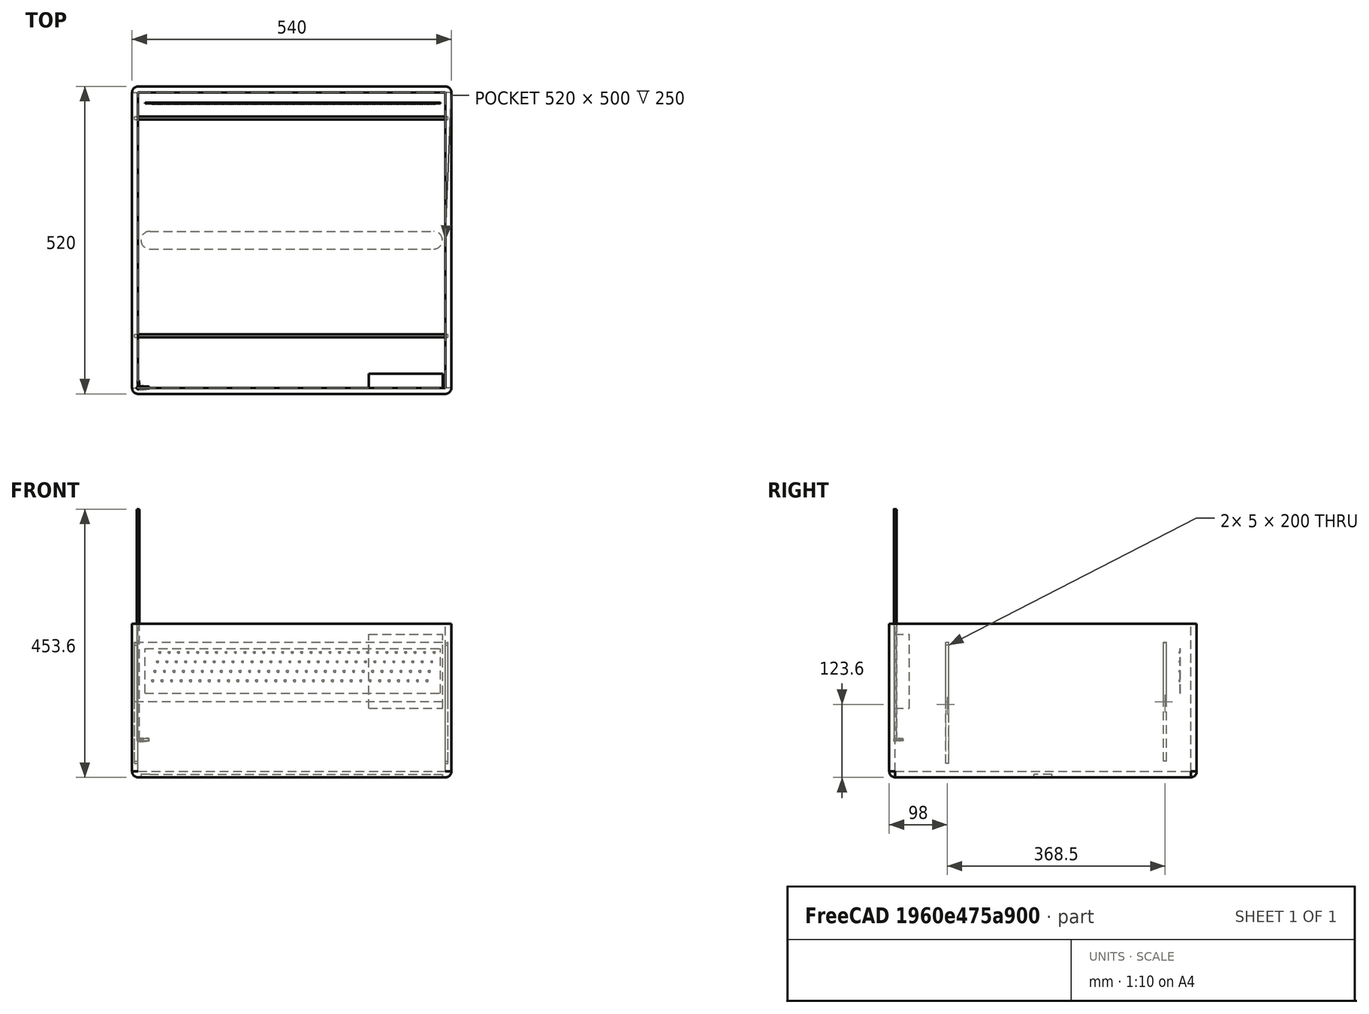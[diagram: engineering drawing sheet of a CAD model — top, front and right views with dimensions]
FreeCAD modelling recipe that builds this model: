
FCSTD DOCUMENT  (FreeCAD 0.20RUnknown)
Label: CherenkovBoxTechnicalNote22February22
License: All rights reserved
LicenseURL: http://en.wikipedia.org/wiki/All_rights_reserved
objects: Part::Part2DObjectPython×16, Part::Box×13, App::Part×13, Part::Compound×10, Part::Sweep×8, App::FeaturePython×7, Part::Feature×6, Part::FeaturePython×4, Part::Cut×3, Part::Thickness×1, Sketcher::SketchObject×1, Part::Extrusion×1
note: 59 computed .brp shape members not serialized (recipe doc carries the construction recipe); baked Part::Feature solids carry a one-line shape summary decoded from their .brp

FEATURE [Part::Box] Box001  label="Support001"
  AttacherType = Attacher::AttachEngine3D
  Height = 100
  Length = 530
  Placement = pos=(-5.7935,85.5,65) rot=(0,0,1;0rad)
  Width = 5
FEATURE [Part::Box] Box002  label="Support002"
  AttacherType = Attacher::AttachEngine3D
  Height = 100
  Length = 530
  Placement = pos=(-5.7935,454,65) rot=(0,0,1;0rad)
  Width = 5
FEATURE [Part::Box] Box008  label="SiPM"
  AttacherType = Attacher::AttachEngine3D
  Height = 3
  Length = 3
  Width = 1
FEATURE [Part::FeaturePython] Array001  label="SiPM001"  # Draft array (typed FeaturePython)
  Angle = 360
  ArrayType = 0
  Axis = (0,0,1)
  Base = -> Box008
  Center = (0,0,0)
  Count = 120
  ExpandArray = false
  Fuse = false
  IntervalAxis = (0,0,0)
  IntervalX = (16,0,0)
  IntervalY = (4,0,16)
  IntervalZ = (0,0,100)
  NumberCircles = 3
  NumberPolar = 5
  NumberX = 30
  NumberY = 4
  NumberZ = 1
  Placement = pos=(23.5,479,98.5) rot=(0,0,1;0rad)
  PlacementList = 120 placements: [(0,0,0),(4,0,16),(8,0,32),(12,0,48),(16,0,0),(20,0,16),(24,0,32),(28,0,48),(32,0,0),(36,0,16),(40,0,32),(44,0,48),(48,0,0),(52,0,16),(56,0,32),(60,0,48),(64,0,0),(68,0,16),(72,0,32),(76,0,48),(80,0,0),(84,0,16),(88,0,32),(92,0,48),(96,0,0),(100,0,16),(104,0,32),(108,0,48),(112,0,0),(116,0,16),(120,0,32),(124,0,48),(128,0,0),(132,0,16),(136,0,32),(140,0,48),(144,0,0),(148,0,16),(152,0,32),+81 more]
  RadialDistance = 50
  ScaleList = (120) [(1,1,1),(1,1,1),(1,1,1),(1,1,1),(1,1,1),(1,1,1),(1,1,1),(1,1,1),(1,1,1),(1,1,1),(1,1,1),(1,1,1),(1,1,1),(1,1,1),(1,1,1),(1,1,1),(1,1,1),(1,1,1),+102 more]
  Symmetry = 1
  TangentialDistance = 25
FEATURE [Part::Box] Box009  label="PCB"
  AttacherType = Attacher::AttachEngine3D
  Height = 75
  Length = 500
  Placement = pos=(11.7065,480,79) rot=(0,0,1;0rad)
  Width = 1
FEATURE [Part::Compound] Compound  label="PCBSiPM"
  Links = -> [Box009,Array001]
  Placement = pos=(0,1.6,0) rot=(0,0,1;0rad)
FEATURE [Part::Feature] Part__Feature003  label="SmallEndCapModel"
  shape: bbox 4.6 x 13 x 4.6 mm, 17 faces (baked)
FEATURE [Part::Feature] Part__Feature004  label="BigEndcapModel"
  shape: bbox 18 x 5.9 x 5.9 mm, 16 faces (baked)
FEATURE [App::Part] SmallEndCap001
  Group = -> [Part__Feature003]
  Origin = -> Origin005
  Placement = pos=(0,0,-8.5) rot=(1,0,0;1.5708rad)
FEATURE [Part::Feature] Part__Feature005  label="StrawTubeModel001"
  shape: bbox 4.15 x 4.15 x 390 mm, 4 faces (baked)
FEATURE [App::Part] StrawTube001
  Group = -> [Part__Feature005]
  Origin = -> Origin
FEATURE [App::Part] BigEndCap001
  Group = -> [Part__Feature004]
  Origin = -> Origin006
  Placement = pos=(0,0,405.5) rot=(0,1,0;1.5708rad)
FEATURE [App::Part] Straw
  Group = -> [StrawTube001,SmallEndCap001,BigEndCap001]
  Origin = -> Origin007
  Placement = pos=(0,0,0) rot=(1,0,0;4.71239rad)
FEATURE [Part::FeaturePython] Array002  label="ArrayStraws"  # Draft array (typed FeaturePython)
  Angle = 360
  ArrayType = 0
  Axis = (0,0,1)
  Base = -> Straw
  Center = (0,0,0)
  Count = 120
  ExpandArray = false
  Fuse = false
  IntervalAxis = (0,0,0)
  IntervalX = (16,0,0)
  IntervalY = (4,0,16)
  IntervalZ = (0,0,100)
  NumberCircles = 3
  NumberPolar = 5
  NumberX = 30
  NumberY = 4
  NumberZ = 1
  Placement = pos=(25,75,100) rot=(0,0,1;0rad)
  PlacementList = <same value as first occurrence — deduplicated (x4 in doc)>
  RadialDistance = 50
  ScaleList = (120) [(1,1,1),(1,1,1),(1,1,1),(1,1,1),(1,1,1),(1,1,1),(1,1,1),(1,1,1),(1,1,1),(1,1,1),(1,1,1),(1,1,1),(1,1,1),(1,1,1),(1,1,1),(1,1,1),(1,1,1),(1,1,1),+102 more]
  Symmetry = 1
  TangentialDistance = 25
FEATURE [Part::Part2DObjectPython] BezCurve004  # Draft 2D object (typed FeaturePython)
  Area = 0
  Closed = false
  Degree = 3
  Length = 133.246
  MakeFace = true
  Points = (4) [(37.73,178.199,85.1424),(15,143.338,83.3527),(-3.29845,149.367,143.96),(39.5292,81.953,149.244)]
FEATURE [Part::Part2DObjectPython] Circle005  # Draft 2D object (typed FeaturePython)
  Area = 0.785398
  FirstAngle = 0
  LastAngle = 0
  MakeFace = true
  Placement = pos=(39.5292,81.953,149.244) rot=(-0.540873,0.659298,0.522286;3.71755rad)
  Radius = 0.5
FEATURE [Part::Part2DObjectPython] BezCurve005  # Draft 2D object (typed FeaturePython)
  Area = 0
  Closed = false
  Degree = 3
  Length = 133.246
  MakeFace = true
  Points = (4) [(37.73,178.199,85.1424),(15,143.338,83.3527),(-3.29845,149.367,143.96),(39.5292,81.953,149.244)]
FEATURE [Part::Box] Box013  label="CalibLEDBox001"
  AttacherType = Attacher::AttachEngine3D
  Height = 25
  Length = 125
  Placement = pos=(390.26,-0.9,53.5) rot=(0.57735,0.57735,0.57735;4.18879rad)
  Width = 125
FEATURE [Part::Part2DObjectPython] BezCurve006  # Draft 2D object (typed FeaturePython)
  Area = 0
  Closed = false
  Degree = 3
  Length = 133.246
  MakeFace = true
  Points = (4) [(37.73,178.199,85.1424),(15,143.338,83.3527),(-3.29845,149.367,143.96),(39.5292,81.953,149.244)]
FEATURE [Part::Part2DObjectPython] Circle006  # Draft 2D object (typed FeaturePython)
  Area = 0.785398
  FirstAngle = 0
  LastAngle = 0
  MakeFace = true
  Placement = pos=(39.5292,81.953,149.244) rot=(-0.540873,0.659298,0.522286;3.71755rad)
  Radius = 0.5
FEATURE [Part::Sweep] Sweep006  label="OpticFiber007"
  Frenet = false
  Placement = pos=(-83.0642,-149.15,32.7197) rot=(-0.889126,-0.323616,-0.323616;1.68804rad)
  Sections = -> [Circle006]
  Solid = false
  Spine = -> BezCurve006 [Edge1]
  Transition = 1
FEATURE [Part::Compound] Compound008  label="Fiber008"
  Links = -> [Sweep006]
  Placement = pos=(538,81,98.5) rot=(0.57735,0.57735,0.57735;4.18879rad)
FEATURE [Part::Part2DObjectPython] BezCurve007  # Draft 2D object (typed FeaturePython)
  Area = 0
  Closed = false
  Degree = 3
  Length = 133.246
  MakeFace = true
  Points = (4) [(37.73,178.199,85.1424),(15,143.338,83.3527),(-3.29845,149.367,143.96),(39.5292,81.953,149.244)]
FEATURE [Part::Sweep] Sweep005  label="OpticFiber006"
  Frenet = false
  Placement = pos=(-83.0642,-149.15,32.7197) rot=(-0.889126,-0.323616,-0.323616;1.68804rad)
  Sections = -> [Circle005]
  Solid = false
  Spine = -> BezCurve007 [Edge1]
  Transition = 1
FEATURE [Part::Compound] Compound007  label="Fiber007"
  Links = -> [Sweep005]
  Placement = pos=(553.7,81,98.2) rot=(0.57735,0.57735,0.57735;4.18879rad)
FEATURE [Part::Part2DObjectPython] Circle007  # Draft 2D object (typed FeaturePython)
  Area = 0.785398
  FirstAngle = 0
  LastAngle = 0
  MakeFace = true
  Placement = pos=(39.5292,81.953,149.244) rot=(-0.540873,0.659298,0.522286;3.71755rad)
  Radius = 0.5
FEATURE [Part::Sweep] Sweep007  label="OpticFiber008"
  Frenet = false
  Placement = pos=(-83.0642,-149.15,32.7197) rot=(-0.889126,-0.323616,-0.323616;1.68804rad)
  Sections = -> [Circle007]
  Solid = false
  Spine = -> BezCurve004 [Edge1]
  Transition = 1
FEATURE [Part::Compound] Compound006  label="Fiber006"
  Links = -> [Sweep007]
  Placement = pos=(558,81,115) rot=(0.57735,0.57735,0.57735;4.18879rad)
FEATURE [Part::Part2DObjectPython] Circle008  # Draft 2D object (typed FeaturePython)
  Area = 0.785398
  FirstAngle = 0
  LastAngle = 0
  MakeFace = true
  Placement = pos=(39.5292,81.953,149.244) rot=(-0.540873,0.659298,0.522286;3.71755rad)
  Radius = 0.5
FEATURE [Part::Sweep] Sweep004  label="OpticFiber005"
  Frenet = false
  Placement = pos=(-83.0642,-149.15,32.7197) rot=(-0.889126,-0.323616,-0.323616;1.68804rad)
  Sections = -> [Circle008]
  Solid = false
  Spine = -> BezCurve005 [Edge1]
  Transition = 1
FEATURE [Part::Compound] Compound005  label="Fiber005"
  Links = -> [Sweep004]
  Placement = pos=(542,81,115) rot=(0.57735,0.57735,0.57735;4.18879rad)
FEATURE [App::Part] Part  label="Fiber"
  Group = -> [Box013,Circle008,BezCurve005,Sweep004,Compound005,Circle007,BezCurve004,Sweep007,Compound006,Sweep005,Circle005,BezCurve007,Compound007,Circle006,Sweep006,BezCurve006,Compound008]
  Origin = -> Origin008
  Placement = pos=(-268.1,0,0) rot=(0,0,1;0rad)
FEATURE [App::Part] Part001  label="SiPMReadout"
  Group = -> [Straw,Array002,Part,Box008,Array001,Box009,Compound,Box002,Box001]
  Origin = -> Origin009
FEATURE [Part::Part2DObjectPython] Circle009  # Draft 2D object (typed FeaturePython)
  Area = 0.785398
  FirstAngle = 0
  LastAngle = 0
  MakeFace = true
  Placement = pos=(39.5292,81.953,149.244) rot=(-0.540873,0.659298,0.522286;3.71755rad)
  Radius = 0.5
FEATURE [Part::Box] Box014  label="SiPM002"
  AttacherType = Attacher::AttachEngine3D
  Height = 3
  Length = 3
  Width = 1
FEATURE [Part::FeaturePython] Array003  label="SiPM003"  # Draft array (typed FeaturePython)
  Angle = 360
  ArrayType = 0
  Axis = (0,0,1)
  Base = -> Box014
  Center = (0,0,0)
  Count = 120
  ExpandArray = false
  Fuse = false
  IntervalAxis = (0,0,0)
  IntervalX = (16,0,0)
  IntervalY = (4,0,16)
  IntervalZ = (0,0,100)
  NumberCircles = 3
  NumberPolar = 5
  NumberX = 30
  NumberY = 4
  NumberZ = 1
  Placement = pos=(23.5,479,98.5) rot=(0,0,1;0rad)
  PlacementList = <same value as first occurrence — deduplicated (x4 in doc)>
  RadialDistance = 50
  ScaleList = (120) [(1,1,1),(1,1,1),(1,1,1),(1,1,1),(1,1,1),(1,1,1),(1,1,1),(1,1,1),(1,1,1),(1,1,1),(1,1,1),(1,1,1),(1,1,1),(1,1,1),(1,1,1),(1,1,1),(1,1,1),(1,1,1),+102 more]
  Symmetry = 1
  TangentialDistance = 25
FEATURE [Part::Part2DObjectPython] Circle010  # Draft 2D object (typed FeaturePython)
  Area = 0.785398
  FirstAngle = 0
  LastAngle = 0
  MakeFace = true
  Placement = pos=(39.5292,81.953,149.244) rot=(-0.540873,0.659298,0.522286;3.71755rad)
  Radius = 0.5
FEATURE [Part::Part2DObjectPython] Circle011  # Draft 2D object (typed FeaturePython)
  Area = 0.785398
  FirstAngle = 0
  LastAngle = 0
  MakeFace = true
  Placement = pos=(39.5292,81.953,149.244) rot=(-0.540873,0.659298,0.522286;3.71755rad)
  Radius = 0.5
FEATURE [Part::Part2DObjectPython] BezCurve008  # Draft 2D object (typed FeaturePython)
  Area = 0
  Closed = false
  Degree = 3
  Length = 133.246
  MakeFace = true
  Points = (4) [(37.73,178.199,85.1424),(15,143.338,83.3527),(-3.29845,149.367,143.96),(39.5292,81.953,149.244)]
FEATURE [Part::Part2DObjectPython] Circle012  # Draft 2D object (typed FeaturePython)
  Area = 0.785398
  FirstAngle = 0
  LastAngle = 0
  MakeFace = true
  Placement = pos=(39.5292,81.953,149.244) rot=(-0.540873,0.659298,0.522286;3.71755rad)
  Radius = 0.5
FEATURE [Part::Part2DObjectPython] BezCurve009  # Draft 2D object (typed FeaturePython)
  Area = 0
  Closed = false
  Degree = 3
  Length = 133.246
  MakeFace = true
  Points = (4) [(37.73,178.199,85.1424),(15,143.338,83.3527),(-3.29845,149.367,143.96),(39.5292,81.953,149.244)]
FEATURE [Part::Sweep] Sweep008  label="OpticFiber009"
  Frenet = false
  Placement = pos=(-83.0642,-149.15,32.7197) rot=(-0.889126,-0.323616,-0.323616;1.68804rad)
  Sections = -> [Circle012]
  Solid = false
  Spine = -> BezCurve009 [Edge1]
  Transition = 1
FEATURE [Part::Compound] Compound009  label="Fiber009"
  Links = -> [Sweep008]
  Placement = pos=(553.7,81,98.2) rot=(0.57735,0.57735,0.57735;4.18879rad)
FEATURE [Part::Box] Box015  label="CalibLEDBox002"
  AttacherType = Attacher::AttachEngine3D
  Height = 25
  Length = 125
  Placement = pos=(390.26,-0.9,53.5) rot=(0.57735,0.57735,0.57735;4.18879rad)
  Width = 125
FEATURE [Part::Part2DObjectPython] BezCurve010  # Draft 2D object (typed FeaturePython)
  Area = 0
  Closed = false
  Degree = 3
  Length = 133.246
  MakeFace = true
  Points = (4) [(37.73,178.199,85.1424),(15,143.338,83.3527),(-3.29845,149.367,143.96),(39.5292,81.953,149.244)]
FEATURE [Part::Sweep] Sweep009  label="OpticFiber010"
  Frenet = false
  Placement = pos=(-83.0642,-149.15,32.7197) rot=(-0.889126,-0.323616,-0.323616;1.68804rad)
  Sections = -> [Circle010]
  Solid = false
  Spine = -> BezCurve010 [Edge1]
  Transition = 1
FEATURE [Part::Compound] Compound010  label="Fiber010"
  Links = -> [Sweep009]
  Placement = pos=(538,81,98.5) rot=(0.57735,0.57735,0.57735;4.18879rad)
FEATURE [Part::Sweep] Sweep010  label="OpticFiber011"
  Frenet = false
  Placement = pos=(-83.0642,-149.15,32.7197) rot=(-0.889126,-0.323616,-0.323616;1.68804rad)
  Sections = -> [Circle011]
  Solid = false
  Spine = -> BezCurve008 [Edge1]
  Transition = 1
FEATURE [Part::Compound] Compound012  label="Fiber012"
  Links = -> [Sweep010]
  Placement = pos=(558,81,115) rot=(0.57735,0.57735,0.57735;4.18879rad)
FEATURE [Part::Part2DObjectPython] BezCurve011  # Draft 2D object (typed FeaturePython)
  Area = 0
  Closed = false
  Degree = 3
  Length = 133.246
  MakeFace = true
  Points = (4) [(37.73,178.199,85.1424),(15,143.338,83.3527),(-3.29845,149.367,143.96),(39.5292,81.953,149.244)]
FEATURE [Part::Sweep] Sweep011  label="OpticFiber012"
  Frenet = false
  Placement = pos=(-83.0642,-149.15,32.7197) rot=(-0.889126,-0.323616,-0.323616;1.68804rad)
  Sections = -> [Circle009]
  Solid = false
  Spine = -> BezCurve011 [Edge1]
  Transition = 1
FEATURE [Part::Compound] Compound011  label="Fiber011"
  Links = -> [Sweep011]
  Placement = pos=(542,81,115) rot=(0.57735,0.57735,0.57735;4.18879rad)
FEATURE [Part::Box] Box016  label="Support003"
  AttacherType = Attacher::AttachEngine3D
  Height = 100
  Length = 530
  Placement = pos=(-5.7935,454,65) rot=(0,0,1;0rad)
  Width = 5
FEATURE [Part::Box] Box017  label="Support004"
  AttacherType = Attacher::AttachEngine3D
  Height = 100
  Length = 530
  Placement = pos=(-5.7935,85.5,65) rot=(0,0,1;0rad)
  Width = 5
FEATURE [App::Part] Part003  label="Fiber013"
  Group = -> [Box015,Circle009,BezCurve011,Sweep011,Compound011,Circle011,BezCurve008,Sweep010,Compound012,Sweep008,Circle012,BezCurve009,Compound009,Circle010,Sweep009,BezCurve010,Compound010]
  Origin = -> Origin012
  Placement = pos=(-112.9,0,0.6) rot=(0,0,1;0rad)
FEATURE [Part::Feature] Part__Feature006  label="SmallEndCapModel001"
  shape: bbox 4.6 x 13 x 4.6 mm, 17 faces (baked)
FEATURE [Part::Feature] Part__Feature007  label="BigEndcapModel001"
  shape: bbox 18 x 5.9 x 5.9 mm, 16 faces (baked)
FEATURE [App::Part] BigEndCap002
  Group = -> [Part__Feature007]
  Origin = -> Origin011
  Placement = pos=(0,0,405.5) rot=(0,1,0;1.5708rad)
FEATURE [Part::Box] Box018  label="PCB001"
  AttacherType = Attacher::AttachEngine3D
  Height = 75
  Length = 500
  Placement = pos=(11.7065,480,79) rot=(0,0,1;0rad)
  Width = 1
FEATURE [Part::Compound] Compound013  label="PCBSiPM001"
  Links = -> [Box018,Array003]
  Placement = pos=(0,1.6,0) rot=(0,0,1;0rad)
FEATURE [App::Part] SmallEndCap002
  Group = -> [Part__Feature006]
  Origin = -> Origin013
  Placement = pos=(0,0,-8.5) rot=(1,0,0;1.5708rad)
FEATURE [Part::Feature] Part__Feature008  label="StrawTubeModel002"
  shape: bbox 4.15 x 4.15 x 390 mm, 4 faces (baked)
FEATURE [App::Part] StrawTube002
  Group = -> [Part__Feature008]
  Origin = -> Origin015
FEATURE [App::Part] Straw001
  Group = -> [StrawTube002,SmallEndCap002,BigEndCap002]
  Origin = -> Origin014
  Placement = pos=(0,0,0) rot=(1,0,0;4.71239rad)
FEATURE [Part::FeaturePython] Array004  label="ArrayStraws001"  # Draft array (typed FeaturePython)
  Angle = 360
  ArrayType = 0
  Axis = (0,0,1)
  Base = -> Straw001
  Center = (0,0,0)
  Count = 120
  ExpandArray = false
  Fuse = false
  IntervalAxis = (0,0,0)
  IntervalX = (16,0,0)
  IntervalY = (4,0,16)
  IntervalZ = (0,0,100)
  NumberCircles = 3
  NumberPolar = 5
  NumberX = 30
  NumberY = 4
  NumberZ = 1
  Placement = pos=(25,75,100) rot=(0,0,1;0rad)
  PlacementList = <same value as first occurrence — deduplicated (x4 in doc)>
  RadialDistance = 50
  ScaleList = (120) [(1,1,1),(1,1,1),(1,1,1),(1,1,1),(1,1,1),(1,1,1),(1,1,1),(1,1,1),(1,1,1),(1,1,1),(1,1,1),(1,1,1),(1,1,1),(1,1,1),(1,1,1),(1,1,1),(1,1,1),(1,1,1),+102 more]
  Symmetry = 1
  TangentialDistance = 25
FEATURE [App::Part] Part002  label="APDReadout"
  Group = -> [Straw001,Array004,Part003,Box014,Array003,Box018,Compound013,Box016,Box017]
  Origin = -> Origin010
  Placement = pos=(0,0,-101.3) rot=(0,0,1;0rad)
FEATURE [Part::Box] Box019  label="SupportRail003"
  AttacherType = Attacher::AttachEngine3D
  Height = 200
  Length = 530
  Placement = pos=(-5.7935,85.5,13.6) rot=(0,0,1;0rad)
  Width = 5
FEATURE [Part::Box] Box020  label="SupportRail004"
  AttacherType = Attacher::AttachEngine3D
  Height = 200
  Length = 530
  Placement = pos=(-5.7935,454,17.5) rot=(0,0,1;0rad)
  Width = 5
FEATURE [Part::Box] Box021  label="Cube003"
  AttacherType = Attacher::AttachEngine3D
  Height = 250
  Length = 520
  Width = 500
FEATURE [Part::Thickness] Thickness001  label="Box001"
  Faces = -> Box021 [Face6]
  Intersection = false
  Join = 0
  Mode = 0
  SelfIntersection = false
  Value = 10
FEATURE [Part::Cut] Cut003
  Base = -> Thickness001
  Tool = -> Box020
FEATURE [Part::Cut] Cut004  label="BoxAll001"
  Base = -> Cut003
  Placement = pos=(0,0,-53.6) rot=(0,0,1;0rad)
  Tool = -> Box019
FEATURE [Sketcher::SketchObject] Sketch
  FullyConstrained = true
  MapMode = 5
  Placement = pos=(0,0,-63.6) rot=(1,0,0;3.14159rad)
  Support = -> [Cut004]
  sketch-geometry (4):
    g0: LineSegment StartX=20 StartY=-235 StartZ=0 EndX=500 EndY=-235 EndZ=0
    g1: LineSegment StartX=20 StartY=-265 StartZ=0 EndX=500 EndY=-265 EndZ=0
    g2: ArcOfCircle CenterX=20 CenterY=-250 CenterZ=0 NormalX=0 NormalY=0 NormalZ=1 AngleXU=0 Radius=15 StartAngle=1.5708 EndAngle=4.71239
    g3: ArcOfCircle CenterX=500 CenterY=-250 CenterZ=0 NormalX=0 NormalY=0 NormalZ=1 AngleXU=0 Radius=15 StartAngle=4.71239 EndAngle=7.85398
  constraints (10):
    c: Horizontal(g0)
    c: Horizontal(g1)
    c: Distance(g0) = 480
    c: Tangent(g3,g0) = 1.5708
    c: Tangent(g2,g0) = 1.5708
    c: Tangent(g2,g1) = -1.5708
    c: Tangent(g3,g1) = -1.5708
    c: Radius(g2) = 15
    c: DistanceX(g-2,g2) = 20
    c: DistanceY(g-1,g2) = -250
FEATURE [Part::Extrusion] Extrude
  Base = -> Sketch
  Dir = (0,0,-1)
  DirMode = 2
  FaceMakerClass = Part::FaceMakerBullseye
  LengthFwd = -5
  LengthRev = 0
  Solid = true
  Symmetric = false
FEATURE [App::FeaturePython] Dimension  label="DimensionCherenkov_X"  # Draft dimension (typed FeaturePython)
  Diameter = false
  Dimline = (500,-50,0)
  Direction = (0,0,0)
  Distance = 540
  End = (530,500,0)
  Normal = (0,0,-1)
  Start = (-10,500,0)
FEATURE [Part::Cut] Cut005  label="Box"
  Base = -> Cut004
  Tool = -> Extrude
FEATURE [App::Part] Part004  label="CherenkovBoxWithStraws"
  Group = -> [Part001,Part002,Thickness001,Sketch,Box020,Box021,Cut004,Extrude,Cut003,Box019,Cut005]
  Origin = -> Origin016
  Placement = pos=(0,0,64) rot=(0,0,1;0rad)
FEATURE [App::FeaturePython] Dimension001  label="DimensionCherenkov_Y"  # Draft dimension (typed FeaturePython)
  Diameter = false
  Dimline = (-100,600,0)
  Direction = (0,0,0)
  Distance = 520
  End = (0,-10,0)
  Normal = (0,0,0)
  Start = (0,510,0)
FEATURE [App::FeaturePython] Dimension002  label="DimensionWindow_Y"  # Draft dimension (typed FeaturePython)
  Diameter = false
  Dimline = (600,600,0)
  Direction = (0,0,0)
  Distance = 50
  End = (425,225,0)
  Normal = (0,0,0)
  Start = (425,275,0)
FEATURE [App::FeaturePython] Dimension003  label="DimensionWindow_X"  # Draft dimension (typed FeaturePython)
  Diameter = false
  Dimline = (600,-100,0)
  Direction = (0,0,0)
  Distance = 400
  End = (460,250,0)
  Normal = (0,0,0)
  Start = (60,250,0)
FEATURE [App::FeaturePython] Dimension004  label="DimensionCherenkov_Z"  # Draft dimension (typed FeaturePython)
  Diameter = false
  Dimline = (0,-50,130)
  Direction = (0,0,0)
  Distance = 260
  End = (0,0,260)
  Normal = (0,0,0)
  Start = (0,0,0)
FEATURE [App::FeaturePython] dLabel  label="StrawLabel"  # WARN: FeaturePython — macro-defined, semantics opaque (R4)
  CustomText = Straws
  LabelType = 0
  Placement = pos=(731.066,434.531,0) rot=(0,0,1;0rad)
  Points = (3) [(731.066,434.531,0),(665.822,434.531,0),(496.498,367.733,197.998)]
  StraightDirection = 0
  StraightDistance = -65.2443
  Target = -> Dimension004
  TargetPoint = (496.498,367.733,197.998)
  Text = Straws
FEATURE [App::FeaturePython] dLabel001  # WARN: FeaturePython — macro-defined, semantics opaque (R4)
  CustomText = LightBox
  LabelType = 0
  Placement = pos=(874.637,53.4528,60.3376) rot=(0.966881,-0.246486,-0.066225;0.217325rad)
  Points = (3) [(874.637,53.4528,60.3376),(754.725,55.8409,54.1358),(374.037,17.4977,141.8)]
  StraightDirection = 0
  StraightDistance = -120.096
  TargetPoint = (374.037,17.4977,141.8)
  Text = LightBox
